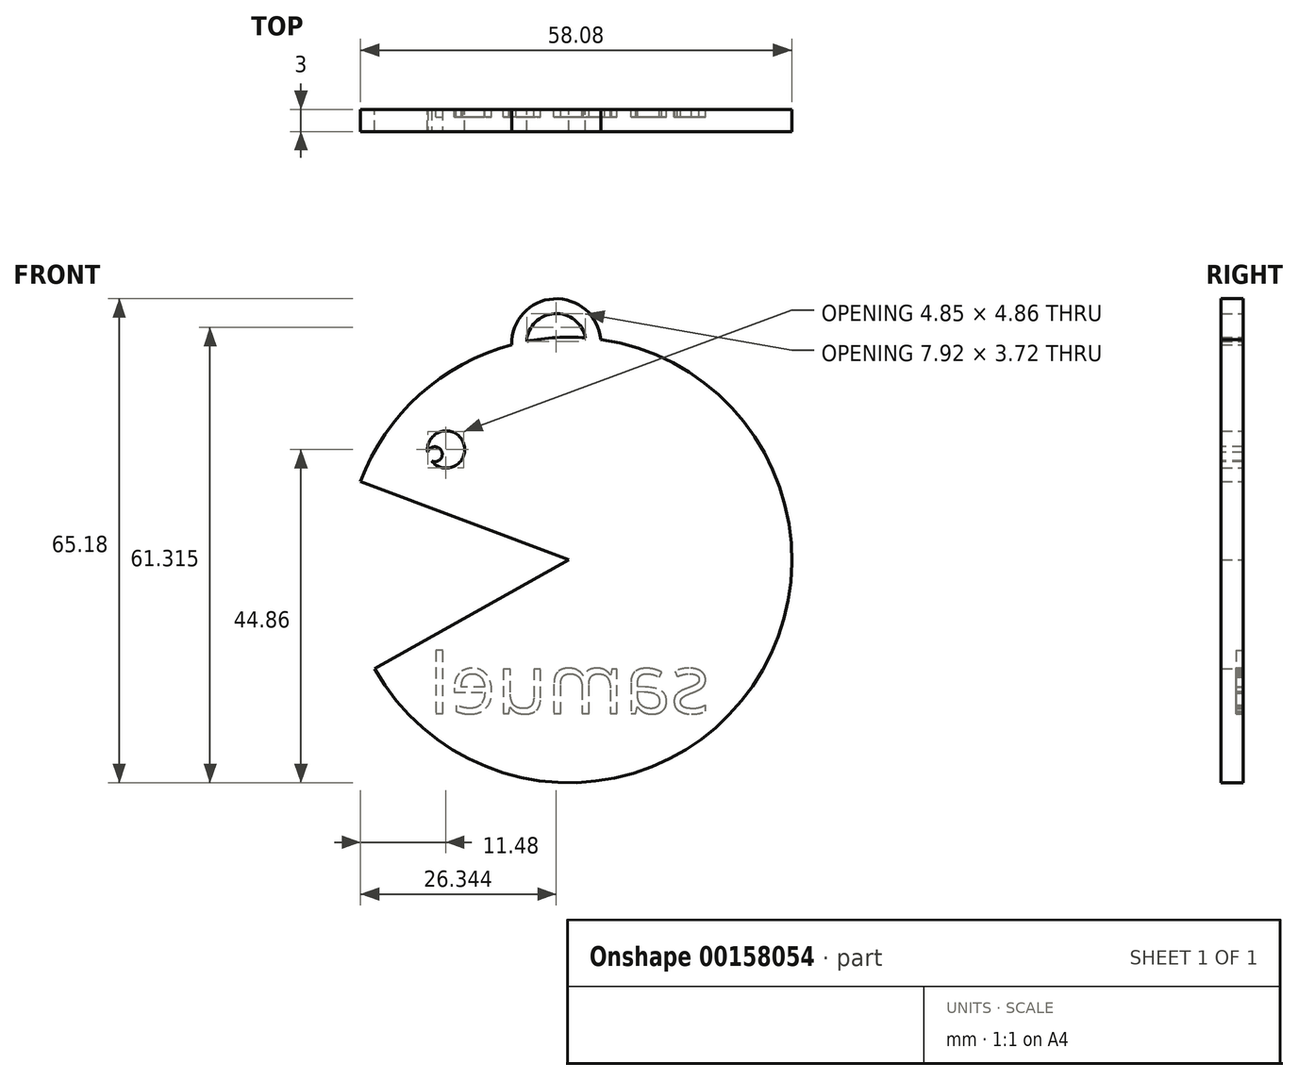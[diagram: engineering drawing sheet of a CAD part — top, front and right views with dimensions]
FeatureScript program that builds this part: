
annotation { "Feature Type Name" : "Feature", "Feature Type Description" : "" }
export const myFeature = defineFeature(function(context is Context, id is Id, definition is map)
    precondition{}
    {
        {
            var Q0;
            Q0=qCreatedBy(makeId("Front.planeOp"),FACE);
            var sketch = newSketch(context, id + "F0", { "sketchPlane" : qUnion([Q0])});
            skCircle(sketch, "E0", {"center": v(27.1, 44.93) * mm, "radius": 2.5 * mm});
            skArc(sketch, "E1", {"start": v(17.47, 15.4) * mm, "mid": v(73.56, 32.33) * mm, "end": v(15.56, 40.59) * mm});
            skLineSegment(sketch, "E2", {"start": v(15.56, 40.59) * mm, "end": v(43.64, 30.05) * mm});
            skLineSegment(sketch, "E3", {"start": v(43.64, 30.05) * mm, "end": v(17.47, 15.4) * mm});
            skArc(sketch, "E4", {"start": v(47.91, 59.75) * mm, "mid": v(41.58, 65.22) * mm, "end": v(35.94, 59.05) * mm});
            skArc(sketch, "E5.0", {"start": v(45.92, 59.58) * mm, "mid": v(41.7, 63.22) * mm, "end": v(37.94, 59.1) * mm});
            skSolve(sketch);
        }
        {
            var Q0;
            Q0 = qSketchRegion(id + "F0", true);
            extrude(context, id + "F1", {"entities" : qUnion([Q0]), "depth" : 3 * mm});
        }
        {
            var Q0;
            Q0=makeQuery(id+"F1.opExtrude","CAP_FACE",FACE,{"disambiguationData":[OSD([sQuery(id+"F0.wireOp",EDGE,"E0"),sQuery(id+"F0.wireOp",EDGE,"E1"),sQuery(id+"F0.wireOp",EDGE,"E2"),sQuery(id+"F0.wireOp",EDGE,"E3"),sQuery(id+"F0.wireOp",EDGE,"E4"),sQuery(id+"F0.wireOp",EDGE,"E5.0")])],"isStart":true});
            var sketch = newSketch(context, id + "F2", { "sketchPlane" : qUnion([Q0])});
            skText(sketch, "E6", { "text": "samuel", "fontName": "OpenSans-Regular.ttf"});
            const initialGuessF2  = {"E6": [-0.0626, 0.0094, 1, 0, 0.00803]};
            skSetInitialGuess(sketch, initialGuessF2);
            skSolve(sketch);
        }
        {
            var Q0;
            Q0 = qSketchRegion(id + "F2", true);
            extrude(context, id + "F3", {"entities" : qUnion([Q0]), "operationType" : NewBodyOperationType.REMOVE, "oppositeDirection" : true, "depth" : 1 * mm});
        }
        {
            var Q0;
            Q0=makeQuery(id+"F1.opExtrude","CAP_FACE",FACE,{"disambiguationData":[OSD([sQuery(id+"F0.wireOp",EDGE,"E0"),sQuery(id+"F0.wireOp",EDGE,"E1"),sQuery(id+"F0.wireOp",EDGE,"E2"),sQuery(id+"F0.wireOp",EDGE,"E3"),sQuery(id+"F0.wireOp",EDGE,"E4"),sQuery(id+"F0.wireOp",EDGE,"E5.0")])],"isStart":false});
            var sketch = newSketch(context, id + "F4", { "sketchPlane" : qUnion([Q0])});
            skCircle(sketch, "E7", {"center": v(25.57, 44.29) * mm, "radius": 1 * mm});
            skSolve(sketch);
        }
        {
            var Q0;
            Q0 = qSketchRegion(id + "F4", true);
            var Q1;
            {var subQ0=sQuery(id+"F0.wireOp",EDGE,"E4");var subQ1=sQuery(id+"F0.wireOp",EDGE,"E5.0");var subQ2=sQuery(id+"F0.wireOp",EDGE,"E1");var subQ3=sQuery(id+"F0.wireOp",EDGE,"E3");var subQ4=sQuery(id+"F0.wireOp",EDGE,"E0");var subQ5=sQuery(id+"F0.wireOp",EDGE,"E2");Q1=makeQuery(id+"F3.boolean.opBoolean","SPLIT",FACE,{"disambiguationData":[TD([makeQuery(id+"F1.opExtrude","SWEPT_FACE",FACE,{"disambiguationData":[OSD([subQ4])]})])],"derivedFrom":makeQuery(id+"F1.opExtrude","CAP_FACE",FACE,{"disambiguationData":[OSD([subQ4,subQ2,subQ5,subQ3,subQ0,subQ1])],"isStart":true})});}
            var Q2;
            Q2=makeQuery(id+"F1.opExtrude","SWEPT_BODY",BODY,{"disambiguationData":[OSD([sQuery(id+"F0.wireOp",EDGE,"E0"),sQuery(id+"F0.wireOp",EDGE,"E1"),sQuery(id+"F0.wireOp",EDGE,"E2"),sQuery(id+"F0.wireOp",EDGE,"E3"),sQuery(id+"F0.wireOp",EDGE,"E4"),sQuery(id+"F0.wireOp",EDGE,"E5.0")])]});
            extrude(context, id + "F5", {"entities" : qUnion([Q0]), "operationType" : NewBodyOperationType.ADD, "endBound" : BoundingType.UP_TO_SURFACE, "oppositeDirection" : true, "endBoundEntityFace" : qUnion([Q1]), "endBoundEntityBody" : qUnion([Q2]), "depth" : 25 * mm});
        }
    });
